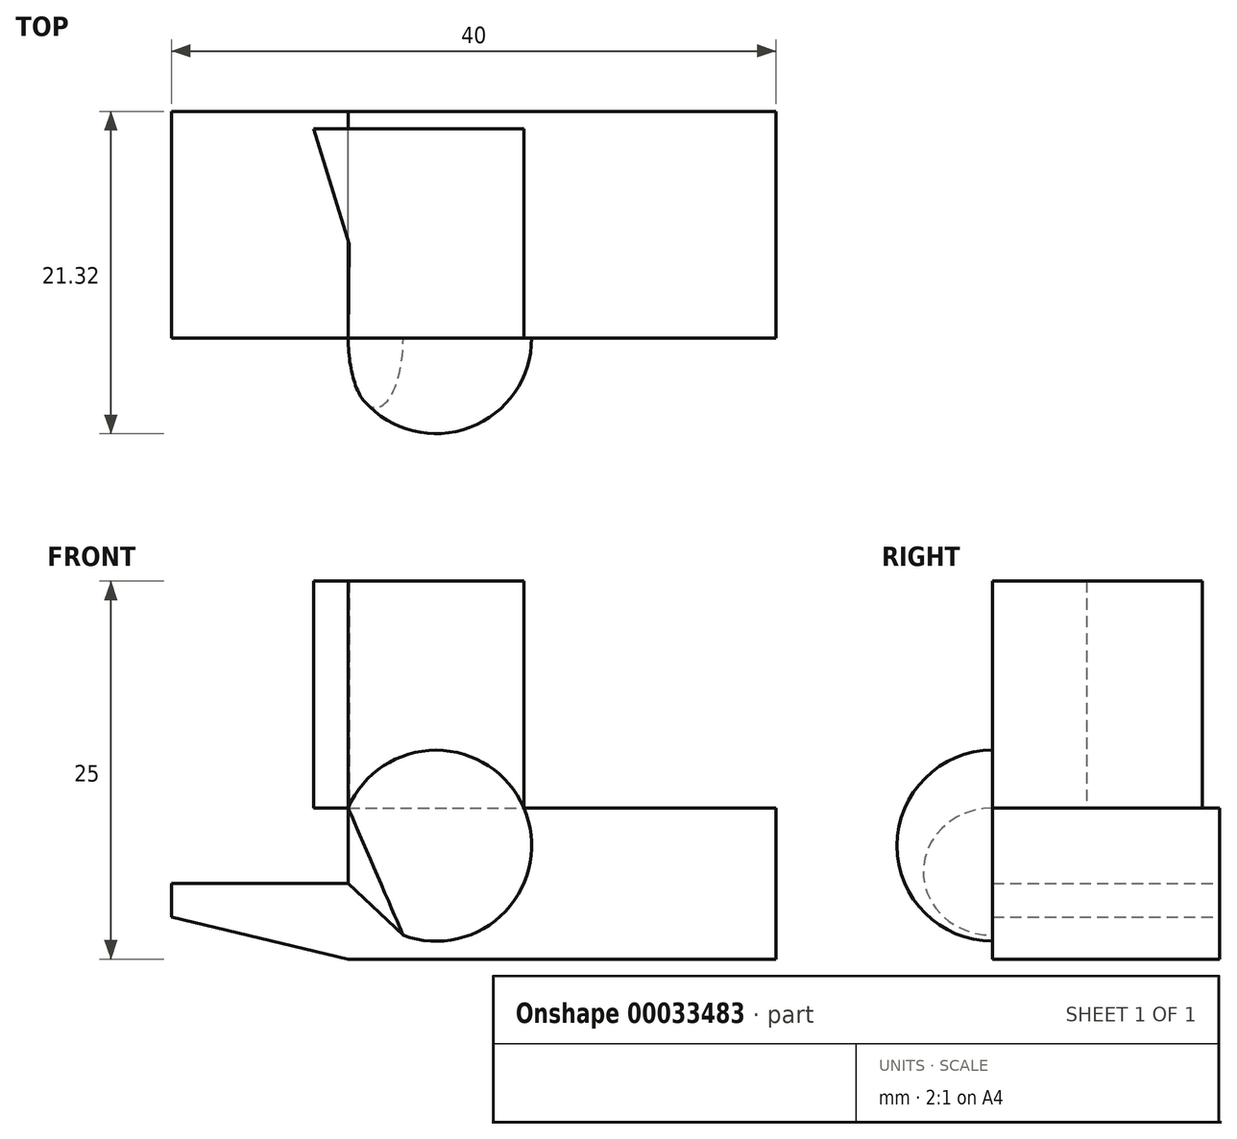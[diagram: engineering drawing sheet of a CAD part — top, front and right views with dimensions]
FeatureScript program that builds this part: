
annotation { "Feature Type Name" : "Feature", "Feature Type Description" : "" }
export const myFeature = defineFeature(function(context is Context, id is Id, definition is map)
    precondition{}
    {
        {
            var Q0;
            Q0=qCreatedBy(makeId("Front.planeOp"),FACE);
            var sketch = newSketch(context, id + "F0", { "sketchPlane" : qUnion([Q0])});
            skLineSegment(sketch, "E0", {"start": v(0, 0) * mm, "end": v(-28.3, 0) * mm});
            skLineSegment(sketch, "E1", {"start": v(-28.3, 5) * mm, "end": v(-28.3, 10) * mm});
            skLineSegment(sketch, "E2", {"start": v(-28.3, 10) * mm, "end": v(-28.3, 5) * mm});
            skLineSegment(sketch, "E3", {"start": v(-28.3, 5) * mm, "end": v(-40, 5) * mm});
            skLineSegment(sketch, "E4", {"start": v(-40, 5) * mm, "end": v(-40, 5) * mm});
            skLineSegment(sketch, "E5", {"start": v(-40, 2.79) * mm, "end": v(-28.3, 0) * mm});
            skLineSegment(sketch, "E6", {"start": v(-40, 5) * mm, "end": v(-40, 2.79) * mm});
            skLineSegment(sketch, "E7", {"start": v(-28.3, 10) * mm, "end": v(0, 10) * mm});
            skLineSegment(sketch, "E8", {"start": v(0, 10) * mm, "end": v(0, 0) * mm});
            skSolve(sketch);
        }
        {
            var Q0;
            Q0 = qSketchRegion(id + "F0", true);
            var Q1;
            Q1=makeQuery(id+"F0.imprint","IMPRINT",FACE,{"disambiguationData":[TD([[makeQuery(id+"F0.imprint","IMPRINT",EDGE,{"derivedFrom":sQuery(id+"F0.wireOp",EDGE,"E0")}),-1.0]])]});
            extrude(context, id + "F1", {"entities" : qUnion([Q0, Q1]), "depth" : 15 * mm});
        }
        {
            var Q0;
            Q0=makeQuery(id+"F1.opExtrude","SWEPT_FACE",FACE,{"disambiguationData":[OSD([sQuery(id+"F0.wireOp",EDGE,"E7")])]});
            var sketch = newSketch(context, id + "F2", { "sketchPlane" : qUnion([Q0])});
            skLineSegment(sketch, "E9", {"start": v(-28.24, -8.78) * mm, "end": v(-30.58, -1.15) * mm});
            skLineSegment(sketch, "E10", {"start": v(-30.58, -1.15) * mm, "end": v(-16.7, -1.15) * mm});
            skLineSegment(sketch, "E11", {"start": v(-16.7, -1.15) * mm, "end": v(-16.7, -15) * mm});
            skLineSegment(sketch, "E12", {"start": v(-16.7, -15) * mm, "end": v(-28.3, -15) * mm});
            skLineSegment(sketch, "E13", {"start": v(-28.3, -15) * mm, "end": v(-28.24, -8.78) * mm});
            skSolve(sketch);
        }
        {
            var Q0;
            Q0 = qSketchRegion(id + "F2", true);
            extrude(context, id + "F3", {"entities" : qUnion([Q0]), "operationType" : NewBodyOperationType.ADD, "depth" : 15 * mm});
        }
        {
            var Q0;
            Q0=makeQuery(id+"F3.boolean.opBoolean","MERGE",FACE,{"derivedFrom":[makeQuery(id+"F1.opExtrude","CAP_FACE",FACE,{"disambiguationData":[OSD([sQuery(id+"F0.wireOp",EDGE,"E0"),sQuery(id+"F0.wireOp",EDGE,"E2"),sQuery(id+"F0.wireOp",EDGE,"E3"),sQuery(id+"F0.wireOp",EDGE,"E5"),sQuery(id+"F0.wireOp",EDGE,"E6"),sQuery(id+"F0.wireOp",EDGE,"E7"),sQuery(id+"F0.wireOp",EDGE,"E8")])],"isStart":false}),makeQuery(id+"F3.opExtrude","SWEPT_FACE",FACE,{"disambiguationData":[OSD([sQuery(id+"F2.wireOp",EDGE,"E12")])]})]});
            var sketch = newSketch(context, id + "F4", { "sketchPlane" : qUnion([Q0])});
            skLineSegment(sketch, "E14", {"start": v(-16.7, 10) * mm, "end": v(-28.3, 5) * mm});
            skArc(sketch, "E15", {"start": v(-16.7, 10) * mm, "mid": v(-25, 13.3) * mm, "end": v(-28.3, 5) * mm});
            skSolve(sketch);
        }
        {
            var Q0;
            {var subQ1=sQuery(id+"F0.wireOp",EDGE,"E2");var subQ2=makeQuery(id+"F1.opExtrude","CAP_EDGE",EDGE,{"disambiguationData":[OSD([subQ1])],"isStart":false});Q0=makeQuery(id+"F4.imprint","IMPRINT",FACE,{"disambiguationData":[TD([[makeQuery(id+"F4.imprint","IMPRINT",EDGE,{"derivedFrom":subQ2}),-1.0]])]});}
            var Q1;
            {var subQ0=sQuery(id+"F4.wireOp",EDGE,"E14");Q1=makeQuery(id+"F4.imprint","IMPRINT",FACE,{"disambiguationData":[TD([[makeQuery(id+"F4.imprint","IMPRINT",EDGE,{"derivedFrom":subQ0}),-1.0]])]});}
            var Q2;
            Q2=sQuery(id+"F4.wireOp",EDGE,"E14");
            revolve(context, id + "F5", {"operationType" : NewBodyOperationType.ADD, "entities" : qUnion([Q0, Q1]), "axis" : qUnion([Q2]), "revolveType" : RevolveType.FULL});
        }
    });
